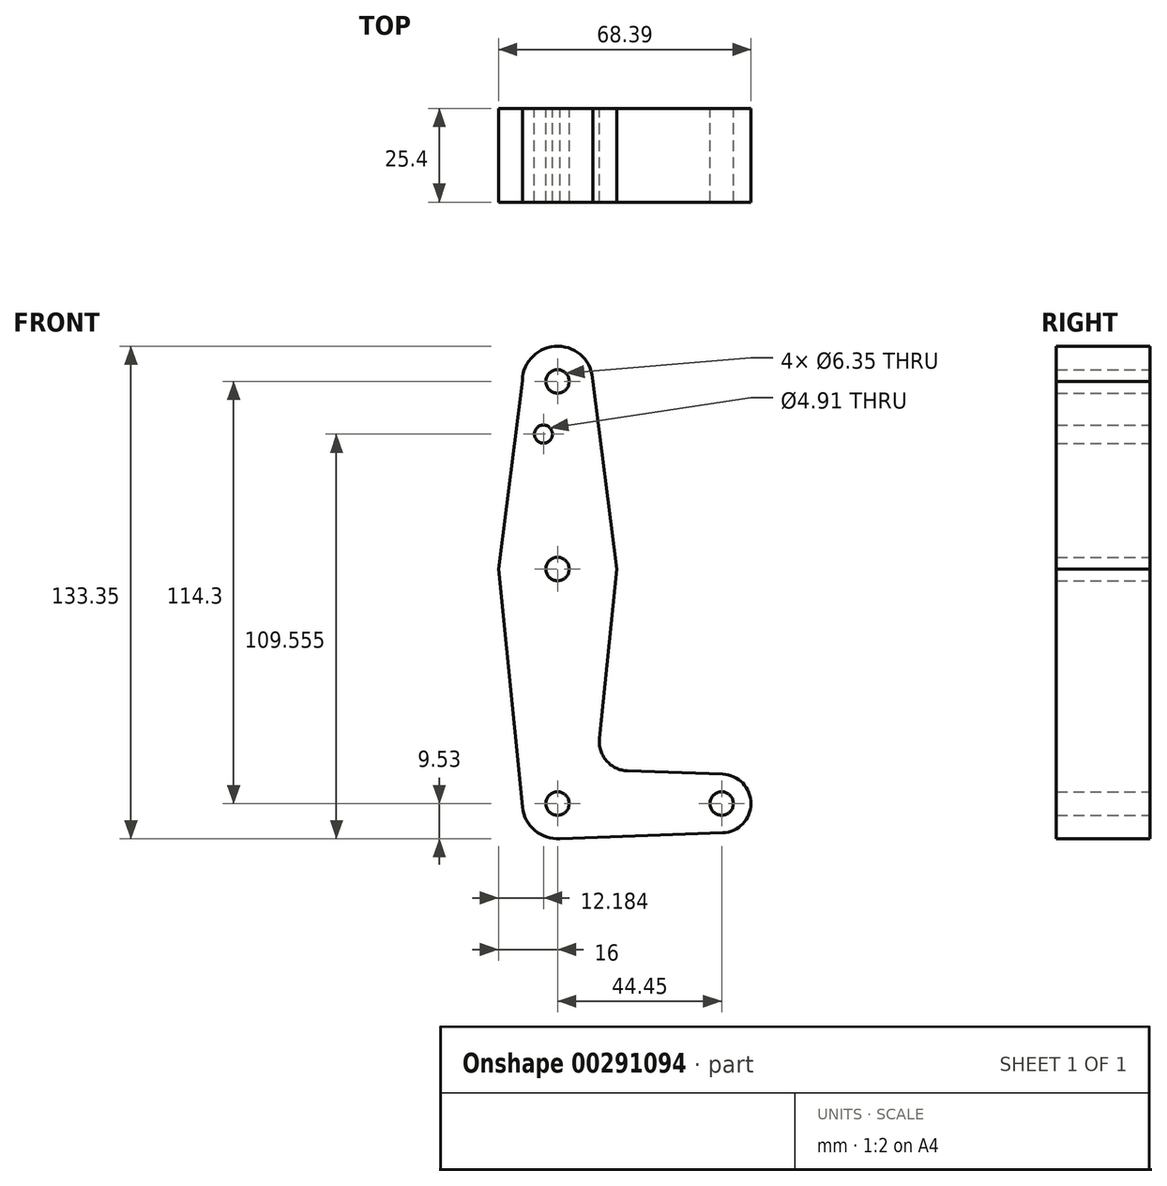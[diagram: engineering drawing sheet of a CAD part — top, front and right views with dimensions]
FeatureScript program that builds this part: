
annotation { "Feature Type Name" : "Feature", "Feature Type Description" : "" }
export const myFeature = defineFeature(function(context is Context, id is Id, definition is map)
    precondition{}
    {
        {
            var Q0;
            Q0=qCreatedBy(makeId("Front.planeOp"),FACE);
            var sketch = newSketch(context, id + "F0", { "sketchPlane" : qUnion([Q0])});
            skLineSegment(sketch, "E0", {"start": v(0, 50.8) * mm, "end": v(0, -63.5) * mm});
            skCircle(sketch, "E1", {"center": v(0, 50.8) * mm, "radius": 9.53 * mm});
            skCircle(sketch, "E2", {"center": v(0, 0) * mm, "radius": 15.88 * mm});
            skCircle(sketch, "E3", {"center": v(0, -63.5) * mm, "radius": 9.53 * mm});
            skLineSegment(sketch, "E4", {"start": v(0, -63.5) * mm, "end": v(44.45, -63.5) * mm});
            skCircle(sketch, "E5", {"center": v(44.45, -63.5) * mm, "radius": 7.94 * mm});
            skLineSegment(sketch, "E6", {"start": v(-9.52, 51.05) * mm, "end": v(-16, 0) * mm});
            skLineSegment(sketch, "E7", {"start": v(-16, 0) * mm, "end": v(-9.48, -64.46) * mm});
            skLineSegment(sketch, "E8", {"start": v(9.53, 50.8) * mm, "end": v(16, 0) * mm});
            skLineSegment(sketch, "E9", {"start": v(16, 0) * mm, "end": v(11.36, -45.9) * mm});
            skLineSegment(sketch, "E10", {"start": v(18.98, -54.65) * mm, "end": v(44.73, -55.57) * mm});
            skLineSegment(sketch, "E11", {"start": v(0, -73.03) * mm, "end": v(44.73, -71.43) * mm});
            skArc(sketch, "E12.filletArc", {"start": v(11.36, -45.9) * mm, "mid": v(13.27, -51.93) * mm, "end": v(18.98, -54.65) * mm});
            skCircle(sketch, "E13", {"center": v(0, 50.8) * mm, "radius": 3.18 * mm});
            skCircle(sketch, "E14", {"center": v(-3.82, 36.53) * mm, "radius": 2.45 * mm});
            skCircle(sketch, "E15", {"center": v(0, 0) * mm, "radius": 3.18 * mm});
            skCircle(sketch, "E16", {"center": v(0, -63.5) * mm, "radius": 3.18 * mm});
            skCircle(sketch, "E17", {"center": v(44.45, -63.5) * mm, "radius": 3.18 * mm});
            skSolve(sketch);
        }
        {
            var Q0;
            Q0 = qSketchRegion(id + "F0", true);
            var Q1;
            {var subQ0=sQuery(id+"F0.wireOp",EDGE,"E3");var subQ1=sQuery(id+"F0.wireOp",EDGE,"E0");var subQ2=makeQuery(id+"F0.imprint","INTERSECT",VERTEX,{"derivedFrom":[subQ1,subQ0]});Q1=makeQuery(id+"F0.imprint","IMPRINT",FACE,{"disambiguationData":[TD([[makeQuery(id+"F0.imprint","IMPRINT",EDGE,{"disambiguationData":[TD([[subQ2,-1.0]])],"derivedFrom":subQ1}),1.0]])]});}
            extrude(context, id + "F1", {"entities" : qUnion([Q0, Q1]), "depth" : 25.4 * mm});
        }
    });
